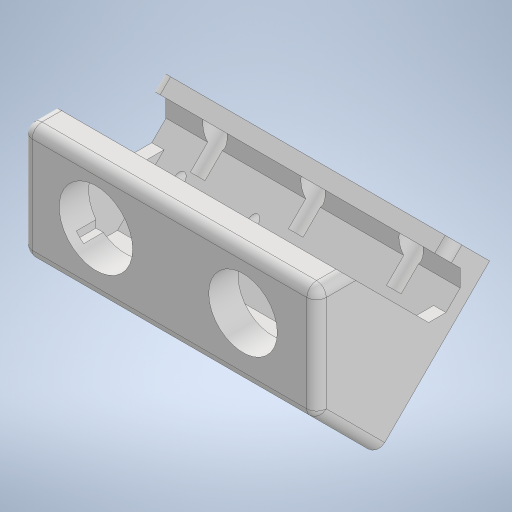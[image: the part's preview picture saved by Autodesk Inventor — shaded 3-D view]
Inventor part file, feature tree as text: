
AUTODESK INVENTOR PART (.ipt)
format: ipt  version: 2024.2 (Build 282272000, 272)  size: 430,592 bytes
history: native  units: in
note: dims shown in document units (in); Inventor stores cm internally (conversion verified against a paired STEP export)
features: extrude x11, sketch x11, projected_geometry x5, chamfer x2, fillet x1, direct_edit x1, move_body x1
ambient origin geometry x8: Origin, YZ Plane, XZ Plane, XY Plane, X Axis, Y Axis, Z Axis, Center Point
bodies: Solid1 (feature_tree)
feature tree (32):
  extrude  "Extrusion1"  Depth=1.1811in
  extrude  "Extrusion2"  Depth=1.1024in
  extrude  "Extrusion3"  Depth=4.3307in
  extrude  "Extrusion4"  Depth=0.9449in
  extrude  "Extrusion5"  Depth=0.315in TaperAngle=0.0deg
  extrude  "Extrusion7"  Depth=1.1811in
  extrude  "Extrusion8"  Depth=0.1299in
  extrude  "Extrusion9"  Depth=0.1299in
  extrude  "Extrusion10"  TaperAngle=45.0deg  [1 undecoded]
  extrude  "Extrusion11"  Depth=0.2362in
  fillet  "Fillet1"  Radius=1.9685in
  chamfer  "Chamfer1"  Distance=0.1969in
  chamfer  "Chamfer2"  Distance=0.2362in
  extrude  "Extrusion12"  Depth=0.1969in TaperAngle=0.0deg
  direct_edit  "Direct Edit1"
  sketch  "Sketch1"  dims[d0=1.7717in d1=1.1811in]
  sketch  "Sketch2"  dims[d4=0.9843in d5=1.1024in]
  projected_geometry  "Projected Loop1"
  sketch  "Sketch3"  dims[d6=2.3622in d7=4.3307in]
  sketch  "Sketch4"  dims[d8=0.1575in d9=0.0in d11=0.9449in]
  projected_geometry  "Projected Loop2"
  sketch  "Sketch5"  dims[d12=0.4724in d13=0.4724in d14=0.315in d15=0.0in]
  sketch  "Sketch7"  dims[d16=1.1811in d17=1.1811in]
  projected_geometry  "Projected Loop3"
  sketch  "Sketch8"  dims[d18=0.1299in d19=0.1299in]
  projected_geometry  "Projected Loop4"
  sketch  "Sketch9"  dims[d20=0.1299in d21=0.1299in]
  sketch  "Sketch10"  dims[d22=0.1969in d23=0.0in d24=45.0deg]
  sketch  "Sketch11"  dims[d25=0.9843in d26=0.2362in d27=1.9685in d28=0.1969in d29=0.0in]
  projected_geometry  "Projected Loop5"
  sketch  "Sketch12"  dims[d30=0.7874in d31=0.2362in d32=0.0in d35=0.1969in d36=0.0in d37=0.1969in d38=0.0in d39=0.1575in d40=0.1575in d41=0.0in d42=0.0in d43=0.2126in d44=0.2126in d45=0.2126in d46=0.3937in d47=0.7874in d48=0.7874in d49=0.3937in d50=0.0in d51=0.3937in d52=0.3937in d53=0.3937in d54=0.5906in d55=0.0394in d56=0.0in d57=0.0in d58=0.1575in d59=0.3937in d60=0.0787in d61=45.0deg d62=0.1969in d63=0.0787in d64=45.0deg d65=0.0in d66=0.0in d67=0.6299in d68=0.0in d69=0.0in d70=-0.0591in]
  move_body  "Move1"
note: 1 required parameter value undecoded (feature->parameter linkage not recoverable at this tier; creation-order binding heuristic only, values carry confidence <= 0.55)
